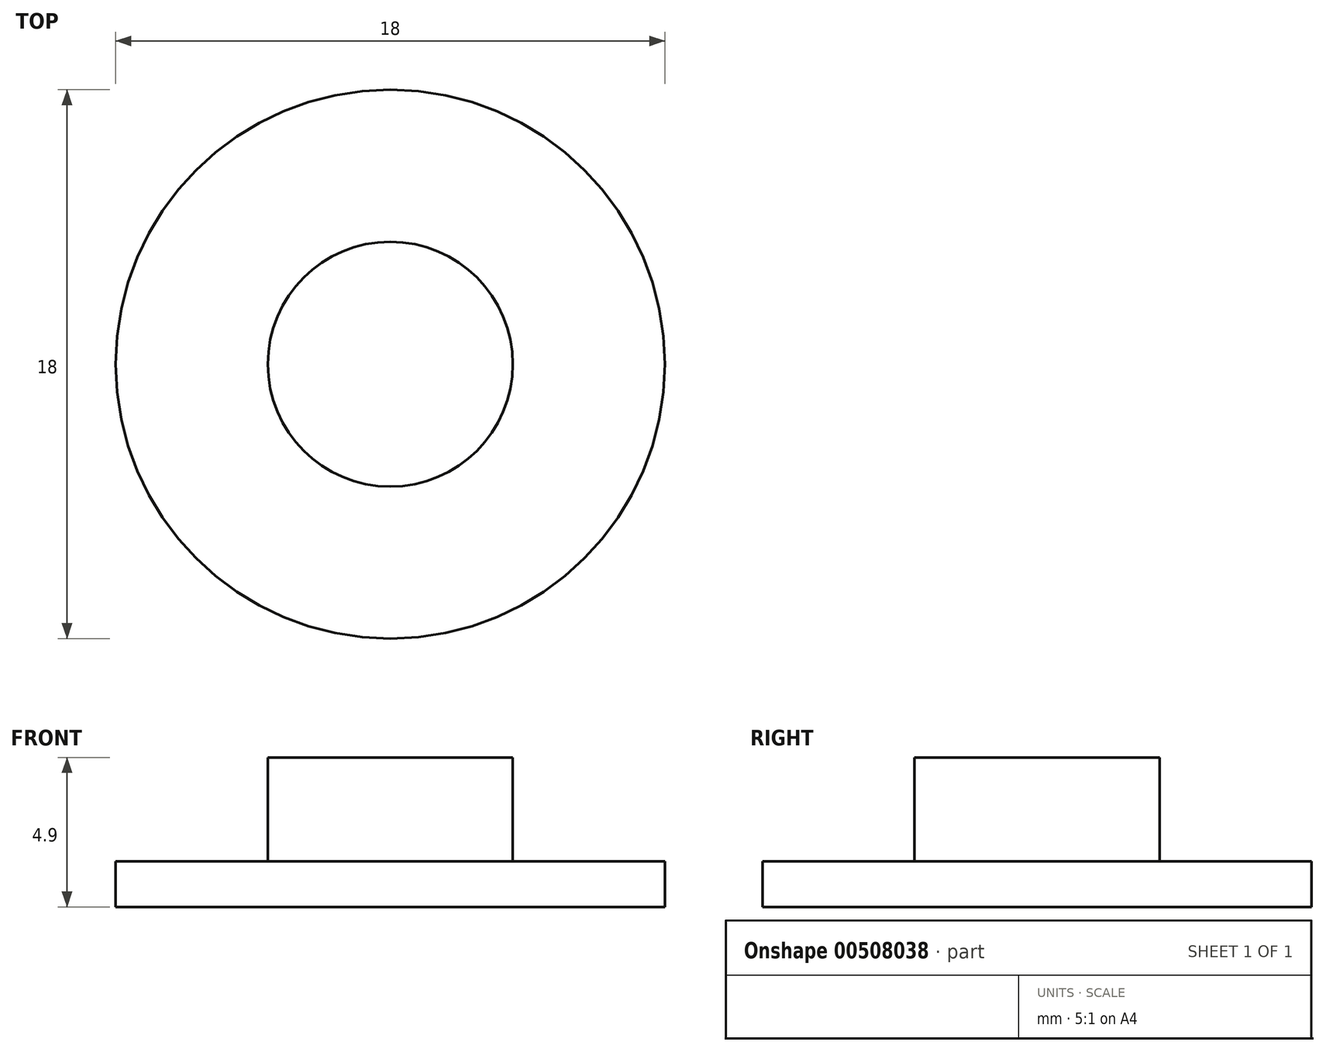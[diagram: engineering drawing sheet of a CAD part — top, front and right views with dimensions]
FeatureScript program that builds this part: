
annotation { "Feature Type Name" : "Feature", "Feature Type Description" : "" }
export const myFeature = defineFeature(function(context is Context, id is Id, definition is map)
    precondition{}
    {
        {
            var Q0;
            Q0=qCreatedBy(makeId("Top.planeOp"),FACE);
            var sketch = newSketch(context, id + "F0", { "sketchPlane" : qUnion([Q0])});
            skCircle(sketch, "E0", {"center": v(0, 0) * mm, "radius": 9 * mm});
            skSolve(sketch);
        }
        {
            var Q0;
            Q0=makeQuery(id+"F0.imprint","IMPRINT",FACE,{"disambiguationData":[TD([[makeQuery(id+"F0.imprint","IMPRINT",EDGE,{"derivedFrom":sQuery(id+"F0.wireOp",EDGE,"E0")}),1.0]])]});
            extrude(context, id + "F1", {"entities" : qUnion([Q0]), "oppositeDirection" : true, "depth" : 1.5 * mm});
        }
        {
            var Q0;
            Q0=makeQuery(id+"F1.opExtrude","CAP_FACE",FACE,{"disambiguationData":[OSD([sQuery(id+"F0.wireOp",EDGE,"E0")])],"isStart":true});
            var sketch = newSketch(context, id + "F2", { "sketchPlane" : qUnion([Q0])});
            skCircle(sketch, "E1", {"center": v(0, 0) * mm, "radius": 4.01 * mm});
            skSolve(sketch);
        }
        {
            var Q0;
            Q0=qSketchRegion(id+"F2",true);
            extrude(context, id + "F3", {"entities" : qUnion([Q0]), "operationType" : NewBodyOperationType.ADD, "depth" : 3.4 * mm});
        }
    });
